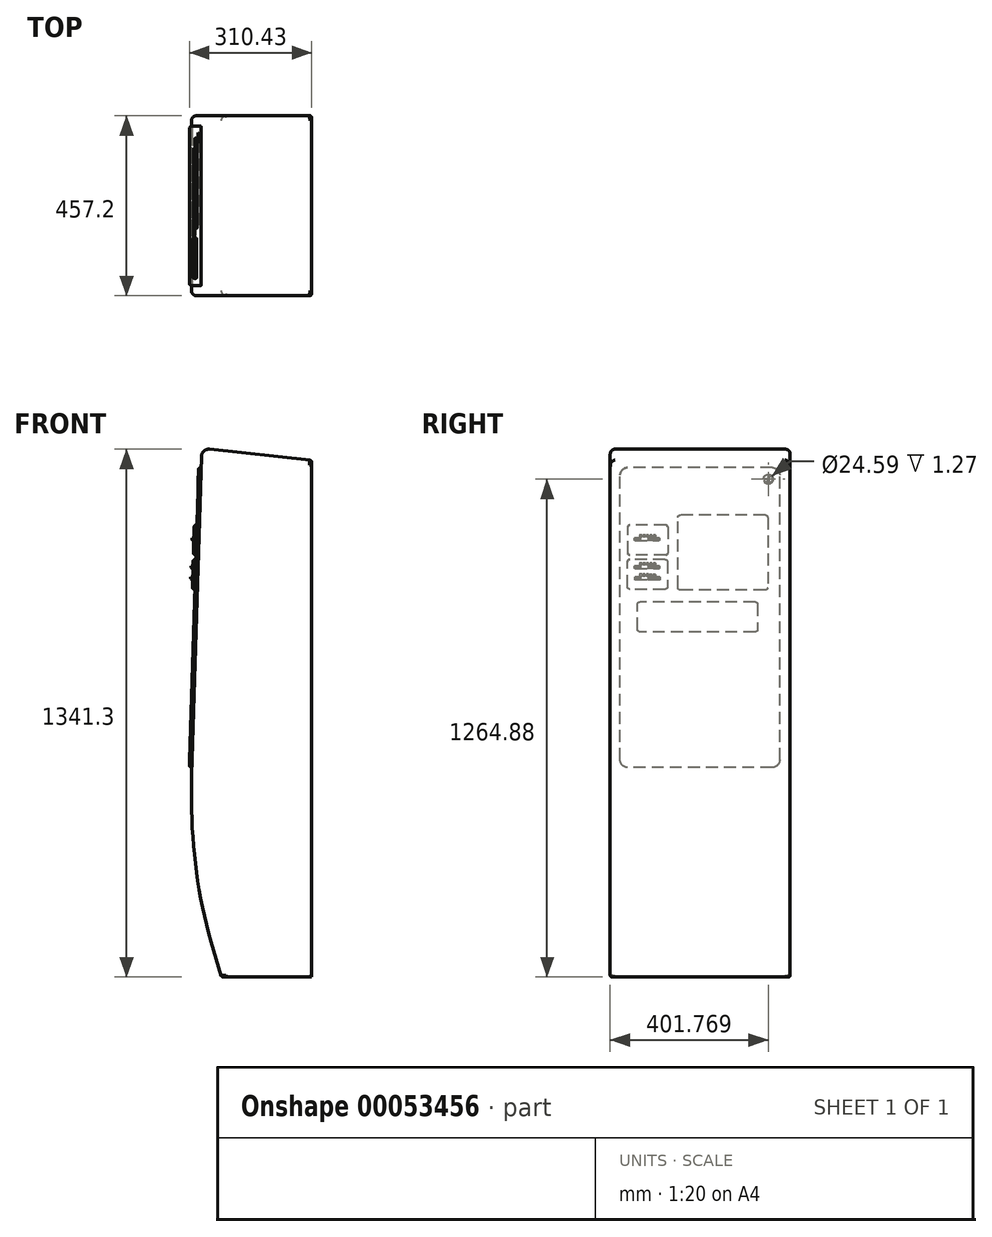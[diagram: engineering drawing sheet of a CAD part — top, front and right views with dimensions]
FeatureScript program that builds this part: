
annotation { "Feature Type Name" : "Feature", "Feature Type Description" : "" }
export const myFeature = defineFeature(function(context is Context, id is Id, definition is map)
    precondition{}
    {
        {
            var Q0;
            Q0=qCreatedBy(makeId("Front.planeOp"),FACE);
            var sketch = newSketch(context, id + "F0", { "sketchPlane" : qUnion([Q0])});
            skLineSegment(sketch, "E0", {"start": v(72.2, -154.9) * mm, "end": v(-156.4, -154.9) * mm});
            skLineSegment(sketch, "E1", {"start": v(72.04, 1157.92) * mm, "end": v(72.2, -154.9) * mm});
            skPoint(sketch, "E2.visualSharp", {"position": v(72.04, 1181.13) * mm});
            skLineSegment(sketch, "E3", {"start": v(-186.8, 1186.28) * mm, "end": v(72.04, 1157.92) * mm});
            skLineSegment(sketch, "E4", {"start": v(72.2, -154.9) * mm, "end": v(72.14, 353.1) * mm});
            skFitSpline(sketch, "E5", {"points": [v(-232.6, 359.2) * mm, v(-156.4, -154.9) * mm], "startDerivative": vector(-16.58, -646.57) * mm, "endDerivative": vector(152.32, -464.69) * mm});
            skLineSegment(sketch, "E6", {"start": v(-232.6, 359.26) * mm, "end": v(-207.9, 1167.93) * mm});
            skPoint(sketch, "E7.orphan", {"position": v(-232.6, 1191.3) * mm});
            skArc(sketch, "E8.filletArc", {"start": v(-232.6, 359.26) * mm, "mid": v(-232.6, 359.2) * mm, "end": v(-232.6, 359.13) * mm});
            skPoint(sketch, "E9.visualSharp", {"position": v(-207.28, 1188.53) * mm});
            skArc(sketch, "E9.filletArc", {"start": v(-186.8, 1186.28) * mm, "mid": v(-201.36, 1181.72) * mm, "end": v(-207.9, 1167.93) * mm});
            skSolve(sketch);
        }
        {
            var Q0;
            Q0=makeQuery(id+"F0.imprint","IMPRINT",FACE,{"disambiguationData":[TD([[makeQuery(id+"F0.imprint","IMPRINT",EDGE,{"derivedFrom":sQuery(id+"F0.wireOp",EDGE,"E0")}),-1.0]])]});
            extrude(context, id + "F1", {"entities" : qUnion([Q0]), "depth" : 457.2 * mm});
        }
        {
            var Q0;
            Q0=makeQuery(id+"F1.opExtrude","SWEPT_FACE",FACE,{"disambiguationData":[OSD([sQuery(id+"F0.wireOp",EDGE,"E6")])]});
            var sketch = newSketch(context, id + "F2", { "sketchPlane" : qUnion([Q0])});
            skLineSegment(sketch, "E10.bottom", {"start": v(45.56, 370.5) * mm, "end": v(412.75, 370.5) * mm});
            skLineSegment(sketch, "E10.top", {"start": v(45.56, 1132.5) * mm, "end": v(412.75, 1132.5) * mm});
            skLineSegment(sketch, "E10.left", {"start": v(26.5, 389.55) * mm, "end": v(26.5, 1113.45) * mm});
            skLineSegment(sketch, "E10.right", {"start": v(431.8, 389.55) * mm, "end": v(431.8, 1113.45) * mm});
            skPoint(sketch, "E11.end.orphan", {"position": v(431.8, 352) * mm});
            skLineSegment(sketch, "E12", {"start": v(0, 1161.04) * mm, "end": v(0, 1135.64) * mm});
            skPoint(sketch, "E13.visualSharp", {"position": v(26.5, 1132.5) * mm});
            skArc(sketch, "E13.filletArc", {"start": v(45.56, 1132.5) * mm, "mid": v(32.09, 1126.92) * mm, "end": v(26.5, 1113.45) * mm});
            skPoint(sketch, "E14.visualSharp", {"position": v(431.8, 1132.5) * mm});
            skArc(sketch, "E14.filletArc", {"start": v(431.8, 1113.45) * mm, "mid": v(426.22, 1126.92) * mm, "end": v(412.75, 1132.5) * mm});
            skPoint(sketch, "E15.visualSharp", {"position": v(431.8, 370.5) * mm});
            skArc(sketch, "E15.filletArc", {"start": v(412.75, 370.5) * mm, "mid": v(426.22, 376.08) * mm, "end": v(431.8, 389.55) * mm});
            skPoint(sketch, "E16.visualSharp", {"position": v(26.5, 370.5) * mm});
            skArc(sketch, "E16.filletArc", {"start": v(26.5, 389.55) * mm, "mid": v(32.09, 376.08) * mm, "end": v(45.56, 370.5) * mm});
            skSolve(sketch);
        }
        {
            var Q0;
            Q0 = qSketchRegion(id + "F2", true);
            extrude(context, id + "F3", {"entities" : qUnion([Q0]), "operationType" : NewBodyOperationType.ADD, "depth" : 6.35 * mm});
        }
        {
            var Q0;
            Q0=makeQuery(id+"F3.opExtrude","CAP_EDGE",EDGE,{"disambiguationData":[OSD([sQuery(id+"F2.wireOp",EDGE,"E10.right")])],"isStart":false});
            fillet(context, id + "F4", {"entities" : qUnion([Q0]), "radius" : 5.08 * mm, "tangentPropagation" : true, "allowEdgeOverflow" : false});
        }
        {
            var Q0;
            Q0=makeQuery(id+"F1.opExtrude","CAP_EDGE",EDGE,{"disambiguationData":[OSD([sQuery(id+"F0.wireOp",EDGE,"E6")])],"isStart":true});
            var Q1;
            Q1=makeQuery(id+"F1.opExtrude","CAP_EDGE",EDGE,{"disambiguationData":[OSD([sQuery(id+"F0.wireOp",EDGE,"E6")])],"isStart":false});
            fillet(context, id + "F5", {"entities" : qUnion([Q0, Q1]), "radius" : 12.7 * mm, "tangentPropagation" : true, "allowEdgeOverflow" : false});
        }
        {
            var Q0;
            Q0=makeQuery(id+"F3.opExtrude","CAP_FACE",FACE,{"disambiguationData":[OSD([sQuery(id+"F2.wireOp",EDGE,"E10.bottom"),sQuery(id+"F2.wireOp",EDGE,"E10.top"),sQuery(id+"F2.wireOp",EDGE,"E10.left"),sQuery(id+"F2.wireOp",EDGE,"E10.right"),sQuery(id+"F2.wireOp",EDGE,"E13.filletArc"),sQuery(id+"F2.wireOp",EDGE,"E14.filletArc"),sQuery(id+"F2.wireOp",EDGE,"E15.filletArc"),sQuery(id+"F2.wireOp",EDGE,"E16.filletArc")])],"isStart":false});
            var sketch = newSketch(context, id + "F6", { "sketchPlane" : qUnion([Q0])});
            skLineSegment(sketch, "E17", {"start": v(31.59, 1113.45) * mm, "end": v(31.59, 389.55) * mm});
            skLineSegment(sketch, "E18", {"start": v(63.34, 1011.85) * mm, "end": v(279.24, 1011.85) * mm});
            skLineSegment(sketch, "E19", {"start": v(56.99, 1005.5) * mm, "end": v(56.99, 827.7) * mm});
            skLineSegment(sketch, "E20", {"start": v(63.34, 821.35) * mm, "end": v(279.24, 821.35) * mm});
            skLineSegment(sketch, "E21", {"start": v(285.59, 827.7) * mm, "end": v(285.59, 1005.5) * mm});
            skLineSegment(sketch, "E22", {"start": v(310.99, 986.45) * mm, "end": v(412.59, 986.45) * mm});
            skLineSegment(sketch, "E23", {"start": v(310.99, 986.45) * mm, "end": v(310.99, 910.25) * mm});
            skLineSegment(sketch, "E24", {"start": v(310.99, 910.25) * mm, "end": v(412.59, 910.25) * mm});
            skLineSegment(sketch, "E25", {"start": v(412.59, 910.25) * mm, "end": v(412.59, 986.45) * mm});
            skLineSegment(sketch, "E26", {"start": v(311.6, 892.88) * mm, "end": v(311.6, 829.38) * mm});
            skLineSegment(sketch, "E27", {"start": v(317.95, 823.03) * mm, "end": v(406.85, 823.03) * mm});
            skLineSegment(sketch, "E28", {"start": v(317.95, 899.23) * mm, "end": v(406.85, 899.23) * mm});
            skLineSegment(sketch, "E29", {"start": v(413.2, 829.38) * mm, "end": v(413.2, 892.88) * mm});
            skLineSegment(sketch, "E30", {"start": v(88.74, 791.2) * mm, "end": v(381.45, 791.2) * mm});
            skLineSegment(sketch, "E31", {"start": v(82.39, 784.84) * mm, "end": v(82.39, 721.34) * mm});
            skLineSegment(sketch, "E32", {"start": v(88.74, 715) * mm, "end": v(381.45, 715) * mm});
            skLineSegment(sketch, "E33", {"start": v(387.8, 721.34) * mm, "end": v(387.8, 784.84) * mm});
            skPoint(sketch, "E34.visualSharp", {"position": v(56.99, 1011.85) * mm});
            skArc(sketch, "E34.filletArc", {"start": v(63.34, 1011.85) * mm, "mid": v(58.85, 1009.99) * mm, "end": v(56.99, 1005.5) * mm});
            skPoint(sketch, "E35.visualSharp", {"position": v(285.59, 1011.85) * mm});
            skArc(sketch, "E35.filletArc", {"start": v(285.59, 1005.5) * mm, "mid": v(283.73, 1009.99) * mm, "end": v(279.24, 1011.85) * mm});
            skPoint(sketch, "E36.visualSharp", {"position": v(285.59, 821.35) * mm});
            skArc(sketch, "E36.filletArc", {"start": v(279.24, 821.35) * mm, "mid": v(283.73, 823.2) * mm, "end": v(285.59, 827.7) * mm});
            skPoint(sketch, "E37.visualSharp", {"position": v(56.99, 821.35) * mm});
            skArc(sketch, "E37.filletArc", {"start": v(56.99, 827.7) * mm, "mid": v(58.85, 823.2) * mm, "end": v(63.34, 821.35) * mm});
            skPoint(sketch, "E38.visualSharp", {"position": v(82.39, 791.2) * mm});
            skArc(sketch, "E38.filletArc", {"start": v(88.74, 791.2) * mm, "mid": v(84.25, 789.33) * mm, "end": v(82.39, 784.84) * mm});
            skPoint(sketch, "E39.visualSharp", {"position": v(82.39, 715) * mm});
            skArc(sketch, "E39.filletArc", {"start": v(82.39, 721.34) * mm, "mid": v(84.25, 716.85) * mm, "end": v(88.74, 715) * mm});
            skPoint(sketch, "E40.visualSharp", {"position": v(387.8, 715) * mm});
            skArc(sketch, "E40.filletArc", {"start": v(381.45, 715) * mm, "mid": v(385.94, 716.85) * mm, "end": v(387.8, 721.34) * mm});
            skPoint(sketch, "E41.visualSharp", {"position": v(387.8, 791.2) * mm});
            skArc(sketch, "E41.filletArc", {"start": v(387.8, 784.84) * mm, "mid": v(385.94, 789.33) * mm, "end": v(381.45, 791.2) * mm});
            skPoint(sketch, "E42.visualSharp", {"position": v(311.6, 823.03) * mm});
            skArc(sketch, "E42.filletArc", {"start": v(311.6, 829.38) * mm, "mid": v(313.46, 824.89) * mm, "end": v(317.95, 823.03) * mm});
            skPoint(sketch, "E43.visualSharp", {"position": v(311.6, 899.23) * mm});
            skArc(sketch, "E43.filletArc", {"start": v(317.95, 899.23) * mm, "mid": v(313.46, 897.37) * mm, "end": v(311.6, 892.88) * mm});
            skPoint(sketch, "E44.visualSharp", {"position": v(413.2, 899.23) * mm});
            skArc(sketch, "E44.filletArc", {"start": v(413.2, 892.88) * mm, "mid": v(411.34, 897.37) * mm, "end": v(406.85, 899.23) * mm});
            skPoint(sketch, "E45.visualSharp", {"position": v(413.2, 823.03) * mm});
            skArc(sketch, "E45.filletArc", {"start": v(406.85, 823.03) * mm, "mid": v(411.34, 824.89) * mm, "end": v(413.2, 829.38) * mm});
            skSolve(sketch);
        }
        {
            var Q0;
            Q0=makeQuery(id+"F6.imprint","IMPRINT",FACE,{"disambiguationData":[TD([[makeQuery(id+"F6.imprint","IMPRINT",EDGE,{"derivedFrom":sQuery(id+"F6.wireOp",EDGE,"E30")}),-1.0]])]});
            var Q1;
            Q1=makeQuery(id+"F6.imprint","IMPRINT",FACE,{"disambiguationData":[TD([[makeQuery(id+"F6.imprint","IMPRINT",EDGE,{"derivedFrom":sQuery(id+"F6.wireOp",EDGE,"E18")}),-1.0]])]});
            extrude(context, id + "F7", {"entities" : qUnion([Q0, Q1]), "operationType" : NewBodyOperationType.REMOVE, "oppositeDirection" : true, "depth" : 2.54 * mm});
        }
        {
            var Q0;
            Q0=makeQuery(id+"F6.imprint","IMPRINT",FACE,{"disambiguationData":[TD([[makeQuery(id+"F6.imprint","IMPRINT",EDGE,{"derivedFrom":sQuery(id+"F6.wireOp",EDGE,"E22")}),-1.0]])]});
            var Q1;
            Q1=makeQuery(id+"F6.imprint","IMPRINT",FACE,{"disambiguationData":[TD([[makeQuery(id+"F6.imprint","IMPRINT",EDGE,{"derivedFrom":sQuery(id+"F6.wireOp",EDGE,"E26")}),1.0]])]});
            extrude(context, id + "F8", {"entities" : qUnion([Q0, Q1]), "operationType" : NewBodyOperationType.ADD, "depth" : 6.35 * mm});
        }
        {
            var Q0;
            Q0=makeQuery(id+"F8.opExtrude","CAP_EDGE",EDGE,{"disambiguationData":[OSD([sQuery(id+"F6.wireOp",EDGE,"E25")])],"isStart":false});
            var Q1;
            Q1=makeQuery(id+"F8.opExtrude","CAP_EDGE",EDGE,{"disambiguationData":[OSD([sQuery(id+"F6.wireOp",EDGE,"E22")])],"isStart":false});
            var Q2;
            Q2=makeQuery(id+"F8.opExtrude","CAP_EDGE",EDGE,{"disambiguationData":[OSD([sQuery(id+"F6.wireOp",EDGE,"E23")])],"isStart":false});
            var Q3;
            Q3=makeQuery(id+"F8.opExtrude","CAP_EDGE",EDGE,{"disambiguationData":[OSD([sQuery(id+"F6.wireOp",EDGE,"E24")])],"isStart":false});
            fillet(context, id + "F9", {"entities" : qUnion([Q0, Q1, Q2, Q3]), "radius" : 5.08 * mm, "tangentPropagation" : true, "allowEdgeOverflow" : false});
        }
        {
            var Q0;
            Q0=makeQuery(id+"F9.opFillet","BLEND_EDGE",EDGE,{"blendedFrom":[makeQuery(id+"F8.opExtrude","CAP_EDGE",EDGE,{"disambiguationData":[OSD([sQuery(id+"F6.wireOp",EDGE,"E22")])],"isStart":false}),makeQuery(id+"F8.opExtrude","CAP_EDGE",EDGE,{"disambiguationData":[OSD([sQuery(id+"F6.wireOp",EDGE,"E25")])],"isStart":false})],"blendedInto":[]});
            var Q1;
            Q1=makeQuery(id+"F9.opFillet","BLEND_EDGE",EDGE,{"blendedFrom":[makeQuery(id+"F8.opExtrude","CAP_EDGE",EDGE,{"disambiguationData":[OSD([sQuery(id+"F6.wireOp",EDGE,"E24")])],"isStart":false}),makeQuery(id+"F8.opExtrude","CAP_EDGE",EDGE,{"disambiguationData":[OSD([sQuery(id+"F6.wireOp",EDGE,"E25")])],"isStart":false})],"blendedInto":[]});
            var Q2;
            Q2=makeQuery(id+"F9.opFillet","BLEND_EDGE",EDGE,{"blendedFrom":[makeQuery(id+"F8.opExtrude","CAP_EDGE",EDGE,{"disambiguationData":[OSD([sQuery(id+"F6.wireOp",EDGE,"E23")])],"isStart":false}),makeQuery(id+"F8.opExtrude","CAP_EDGE",EDGE,{"disambiguationData":[OSD([sQuery(id+"F6.wireOp",EDGE,"E24")])],"isStart":false})],"blendedInto":[]});
            var Q3;
            Q3=makeQuery(id+"F9.opFillet","BLEND_EDGE",EDGE,{"blendedFrom":[makeQuery(id+"F8.opExtrude","CAP_EDGE",EDGE,{"disambiguationData":[OSD([sQuery(id+"F6.wireOp",EDGE,"E22")])],"isStart":false}),makeQuery(id+"F8.opExtrude","CAP_EDGE",EDGE,{"disambiguationData":[OSD([sQuery(id+"F6.wireOp",EDGE,"E23")])],"isStart":false})],"blendedInto":[]});
            fillet(context, id + "F10", {"entities" : qUnion([Q0, Q1, Q2, Q3]), "radius" : 5.08 * mm, "tangentPropagation" : true, "allowEdgeOverflow" : false});
        }
        {
            var Q0;
            Q0=makeQuery(id+"F8.opExtrude","CAP_EDGE",EDGE,{"disambiguationData":[OSD([sQuery(id+"F6.wireOp",EDGE,"E29")])],"isStart":false});
            var Q1;
            Q1=makeQuery(id+"F8.opExtrude","CAP_EDGE",EDGE,{"disambiguationData":[OSD([sQuery(id+"F6.wireOp",EDGE,"E28")])],"isStart":false});
            var Q2;
            Q2=makeQuery(id+"F8.opExtrude","CAP_EDGE",EDGE,{"disambiguationData":[OSD([sQuery(id+"F6.wireOp",EDGE,"E26")])],"isStart":false});
            var Q3;
            Q3=makeQuery(id+"F8.opExtrude","CAP_EDGE",EDGE,{"disambiguationData":[OSD([sQuery(id+"F6.wireOp",EDGE,"E27")])],"isStart":false});
            fillet(context, id + "F11", {"entities" : qUnion([Q0, Q1, Q2, Q3]), "radius" : 5.08 * mm, "tangentPropagation" : true, "allowEdgeOverflow" : false});
        }
        {
            var Q0;
            Q0=makeQuery(id+"F8.opExtrude","CAP_FACE",FACE,{"disambiguationData":[OSD([sQuery(id+"F6.wireOp",EDGE,"E22"),sQuery(id+"F6.wireOp",EDGE,"E23"),sQuery(id+"F6.wireOp",EDGE,"E24"),sQuery(id+"F6.wireOp",EDGE,"E25")])],"isStart":false});
            var sketch = newSketch(context, id + "F12", { "sketchPlane" : qUnion([Q0])});
            skLineSegment(sketch, "E46", {"start": v(331.8, 952.84) * mm, "end": v(395.3, 952.84) * mm});
            skLineSegment(sketch, "E47", {"start": v(331.8, 946.5) * mm, "end": v(395.3, 946.5) * mm});
            skLineSegment(sketch, "E48", {"start": v(395.3, 946.5) * mm, "end": v(395.3, 952.84) * mm});
            skLineSegment(sketch, "E49", {"start": v(331.8, 952.84) * mm, "end": v(331.8, 946.5) * mm});
            skPoint(sketch, "E50.startSnap0", {"position": v(331.8, 949.67) * mm});
            skLineSegment(sketch, "E51.bottom", {"start": v(332.73, 951.82) * mm, "end": v(394.27, 951.82) * mm});
            skLineSegment(sketch, "E51.top", {"start": v(332.73, 947.35) * mm, "end": v(394.27, 947.35) * mm});
            skLineSegment(sketch, "E51.left", {"start": v(332.73, 951.82) * mm, "end": v(332.73, 947.35) * mm});
            skLineSegment(sketch, "E51.right", {"start": v(394.27, 951.82) * mm, "end": v(394.27, 947.35) * mm});
            skSolve(sketch);
        }
        {
            var Q0;
            Q0=makeQuery(id+"F8.opExtrude","CAP_FACE",FACE,{"disambiguationData":[OSD([sQuery(id+"F6.wireOp",EDGE,"E26"),sQuery(id+"F6.wireOp",EDGE,"E27"),sQuery(id+"F6.wireOp",EDGE,"E28"),sQuery(id+"F6.wireOp",EDGE,"E29"),sQuery(id+"F6.wireOp",EDGE,"E42.filletArc"),sQuery(id+"F6.wireOp",EDGE,"E43.filletArc"),sQuery(id+"F6.wireOp",EDGE,"E44.filletArc"),sQuery(id+"F6.wireOp",EDGE,"E45.filletArc")])],"isStart":false});
            var sketch = newSketch(context, id + "F13", { "sketchPlane" : qUnion([Q0])});
            skLineSegment(sketch, "E52", {"start": v(331.36, 881.57) * mm, "end": v(394.86, 881.57) * mm});
            skLineSegment(sketch, "E53", {"start": v(331.36, 875.22) * mm, "end": v(394.86, 875.22) * mm});
            skLineSegment(sketch, "E54", {"start": v(394.86, 875.22) * mm, "end": v(394.86, 881.57) * mm});
            skLineSegment(sketch, "E55", {"start": v(331.36, 881.57) * mm, "end": v(331.36, 875.22) * mm});
            skPoint(sketch, "E56.startSnap0", {"position": v(331.36, 878.4) * mm});
            skLineSegment(sketch, "E57.bottom", {"start": v(332.28, 880.55) * mm, "end": v(393.83, 880.55) * mm});
            skLineSegment(sketch, "E57.top", {"start": v(332.28, 876.08) * mm, "end": v(393.83, 876.08) * mm});
            skLineSegment(sketch, "E57.left", {"start": v(332.28, 880.55) * mm, "end": v(332.28, 876.08) * mm});
            skLineSegment(sketch, "E57.right", {"start": v(393.83, 880.55) * mm, "end": v(393.83, 876.08) * mm});
            skLineSegment(sketch, "E58", {"start": v(331.2, 853.46) * mm, "end": v(394.7, 853.46) * mm});
            skLineSegment(sketch, "E59", {"start": v(331.2, 847.11) * mm, "end": v(394.7, 847.11) * mm});
            skLineSegment(sketch, "E60", {"start": v(394.7, 847.11) * mm, "end": v(394.7, 853.46) * mm});
            skLineSegment(sketch, "E61", {"start": v(331.2, 853.46) * mm, "end": v(331.2, 847.11) * mm});
            skPoint(sketch, "E62.startSnap0", {"position": v(331.2, 850.29) * mm});
            skLineSegment(sketch, "E63.bottom", {"start": v(332.13, 852.44) * mm, "end": v(393.68, 852.44) * mm});
            skLineSegment(sketch, "E63.top", {"start": v(332.13, 847.97) * mm, "end": v(393.68, 847.97) * mm});
            skLineSegment(sketch, "E63.left", {"start": v(332.13, 852.44) * mm, "end": v(332.13, 847.97) * mm});
            skLineSegment(sketch, "E63.right", {"start": v(393.68, 852.44) * mm, "end": v(393.68, 847.97) * mm});
            skSolve(sketch);
        }
        {
            var Q0;
            Q0 = qSketchRegion(id + "F12", true);
            extrude(context, id + "F14", {"entities" : qUnion([Q0]), "operationType" : NewBodyOperationType.ADD, "depth" : 5.08 * mm});
        }
        {
            var Q0;
            Q0 = qSketchRegion(id + "F13", true);
            extrude(context, id + "F15", {"entities" : qUnion([Q0]), "operationType" : NewBodyOperationType.ADD, "depth" : 5.08 * mm});
        }
        {
            var Q0;
            Q0=makeQuery(id+"F14.opExtrude","CAP_EDGE",EDGE,{"disambiguationData":[OSD([sQuery(id+"F12.wireOp",EDGE,"E47")])],"isStart":false});
            fillet(context, id + "F16", {"entities" : qUnion([Q0]), "radius" : 5.08 * mm, "tangentPropagation" : true, "allowEdgeOverflow" : false});
        }
        {
            var Q0;
            Q0=makeQuery(id+"F15.opExtrude","CAP_EDGE",EDGE,{"disambiguationData":[OSD([sQuery(id+"F13.wireOp",EDGE,"E53")])],"isStart":false});
            fillet(context, id + "F17", {"entities" : qUnion([Q0]), "radius" : 5.08 * mm, "tangentPropagation" : true, "allowEdgeOverflow" : false});
        }
        {
            var Q0;
            Q0=makeQuery(id+"F15.opExtrude","CAP_EDGE",EDGE,{"disambiguationData":[OSD([sQuery(id+"F13.wireOp",EDGE,"E59")])],"isStart":false});
            var Q1;
            Q1=makeQuery(id+"F1.opExtrude","CAP_FACE",FACE,{"disambiguationData":[OSD([sQuery(id+"F0.wireOp",EDGE,"E0"),sQuery(id+"F0.wireOp",EDGE,"E1"),sQuery(id+"F0.wireOp",EDGE,"E3"),sQuery(id+"F0.wireOp",EDGE,"E4"),sQuery(id+"F0.wireOp",EDGE,"E5"),sQuery(id+"F0.wireOp",EDGE,"E6"),sQuery(id+"F0.wireOp",EDGE,"E8.filletArc"),sQuery(id+"F0.wireOp",EDGE,"E9.filletArc")])],"isStart":false});
            fillet(context, id + "F18", {"entities" : qUnion([Q0, Q1]), "radius" : 5.08 * mm, "tangentPropagation" : true, "allowEdgeOverflow" : false});
        }
        {
            var Q0;
            Q0=makeQuery(id+"F3.opExtrude","CAP_FACE",FACE,{"disambiguationData":[OSD([sQuery(id+"F2.wireOp",EDGE,"E10.bottom"),sQuery(id+"F2.wireOp",EDGE,"E10.top"),sQuery(id+"F2.wireOp",EDGE,"E10.left"),sQuery(id+"F2.wireOp",EDGE,"E10.right"),sQuery(id+"F2.wireOp",EDGE,"E13.filletArc"),sQuery(id+"F2.wireOp",EDGE,"E14.filletArc"),sQuery(id+"F2.wireOp",EDGE,"E15.filletArc"),sQuery(id+"F2.wireOp",EDGE,"E16.filletArc")])],"isStart":false});
            var sketch = newSketch(context, id + "F19", { "sketchPlane" : qUnion([Q0])});
            skCircle(sketch, "E64", {"center": v(55.43, 1102.9) * mm, "radius": 12.3 * mm});
            skArc(sketch, "E65", {"start": v(55.43, 1114.1) * mm, "mid": v(47.9, 1094.72) * mm, "end": v(67.03, 1102.9) * mm});
            skArc(sketch, "E66", {"start": v(55.43, 1113.61) * mm, "mid": v(48.4, 1095.51) * mm, "end": v(66.35, 1102.9) * mm});
            skLineSegment(sketch, "E67", {"start": v(55.43, 1114.1) * mm, "end": v(55.43, 1113.61) * mm});
            skLineSegment(sketch, "E68", {"start": v(66.35, 1102.9) * mm, "end": v(56.55, 1102.9) * mm});
            skLineSegment(sketch, "E69", {"start": v(56.55, 1102.9) * mm, "end": v(56.55, 1103.59) * mm});
            skLineSegment(sketch, "E70", {"start": v(56.55, 1103.59) * mm, "end": v(66.96, 1103.59) * mm});
            skLineSegment(sketch, "E71", {"start": v(66.96, 1103.59) * mm, "end": v(67.03, 1102.9) * mm});
            skLineSegment(sketch, "E72", {"start": v(54.5, 1110.92) * mm, "end": v(54.5, 1097.18) * mm});
            skLineSegment(sketch, "E73", {"start": v(54.5, 1097.18) * mm, "end": v(59.02, 1097.18) * mm});
            skLineSegment(sketch, "E74", {"start": v(59.02, 1097.18) * mm, "end": v(59.02, 1098.24) * mm});
            skLineSegment(sketch, "E75", {"start": v(59.02, 1098.24) * mm, "end": v(55.48, 1098.24) * mm});
            skLineSegment(sketch, "E76", {"start": v(55.48, 1098.24) * mm, "end": v(55.48, 1110.92) * mm});
            skCircle(sketch, "E77", {"center": v(51.16, 1109.43) * mm, "radius": 1.49 * mm});
            skLineSegment(sketch, "E78", {"start": v(54.5, 1110.92) * mm, "end": v(55.48, 1110.92) * mm});
            skSolve(sketch);
        }
        {
            var Q0;
            Q0 = qSketchRegion(id + "F19", true);
            extrude(context, id + "F20", {"entities" : qUnion([Q0]), "operationType" : NewBodyOperationType.REMOVE, "oppositeDirection" : true, "depth" : 1.27 * mm});
        }
        {
            var Q0;
            {var subQ0=sQuery(id+"F6.wireOp",EDGE,"E24");var subQ1=sQuery(id+"F6.wireOp",EDGE,"E25");var subQ3=sQuery(id+"F6.wireOp",EDGE,"E22");var subQ5=sQuery(id+"F6.wireOp",EDGE,"E23");Q0=makeQuery(id+"F14.boolean.opBoolean","SPLIT",FACE,{"disambiguationData":[TD([makeQuery(id+"F9.opFillet","BLEND_FACE",FACE,{"disambiguationData":[OSD([subQ3])]})])],"derivedFrom":makeQuery(id+"F8.opExtrude","CAP_FACE",FACE,{"disambiguationData":[OSD([subQ3,subQ5,subQ0,subQ1])],"isStart":false})});}
            var sketch = newSketch(context, id + "F21", { "sketchPlane" : qUnion([Q0])});
            skLineSegment(sketch, "E79.bottom", {"start": v(342.05, 960.67) * mm, "end": v(347.53, 960.67) * mm});
            skLineSegment(sketch, "E79.top", {"start": v(342.05, 955.2) * mm, "end": v(347.53, 955.2) * mm});
            skLineSegment(sketch, "E79.left", {"start": v(342.05, 960.67) * mm, "end": v(342.05, 955.2) * mm});
            skLineSegment(sketch, "E79.right", {"start": v(347.53, 960.67) * mm, "end": v(347.53, 955.2) * mm});
            skLineSegment(sketch, "E80.bottom", {"start": v(350.72, 960.67) * mm, "end": v(356.66, 960.67) * mm});
            skLineSegment(sketch, "E80.top", {"start": v(350.72, 955.2) * mm, "end": v(356.66, 955.2) * mm});
            skLineSegment(sketch, "E80.left", {"start": v(350.72, 960.67) * mm, "end": v(350.72, 955.2) * mm});
            skLineSegment(sketch, "E80.right", {"start": v(356.66, 960.67) * mm, "end": v(356.66, 955.2) * mm});
            skLineSegment(sketch, "E81.bottom", {"start": v(359.4, 961.13) * mm, "end": v(365.1, 961.13) * mm});
            skLineSegment(sketch, "E81.top", {"start": v(359.4, 955.42) * mm, "end": v(365.1, 955.42) * mm});
            skLineSegment(sketch, "E81.left", {"start": v(359.4, 961.13) * mm, "end": v(359.4, 955.42) * mm});
            skLineSegment(sketch, "E81.right", {"start": v(365.1, 961.13) * mm, "end": v(365.1, 955.42) * mm});
            skLineSegment(sketch, "E82.bottom", {"start": v(368.06, 961.13) * mm, "end": v(373.54, 961.13) * mm});
            skLineSegment(sketch, "E82.top", {"start": v(368.06, 955.65) * mm, "end": v(373.54, 955.65) * mm});
            skLineSegment(sketch, "E82.left", {"start": v(368.06, 961.13) * mm, "end": v(368.06, 955.65) * mm});
            skLineSegment(sketch, "E82.right", {"start": v(373.54, 961.13) * mm, "end": v(373.54, 955.65) * mm});
            skLineSegment(sketch, "E83.bottom", {"start": v(376.28, 961.13) * mm, "end": v(382.44, 961.13) * mm});
            skLineSegment(sketch, "E83.top", {"start": v(376.28, 955.42) * mm, "end": v(382.44, 955.42) * mm});
            skLineSegment(sketch, "E83.left", {"start": v(376.28, 961.13) * mm, "end": v(376.28, 955.42) * mm});
            skLineSegment(sketch, "E83.right", {"start": v(382.44, 961.13) * mm, "end": v(382.44, 955.42) * mm});
            skLineSegment(sketch, "E84.bottom", {"start": v(342, 889.9) * mm, "end": v(347.48, 889.9) * mm});
            skLineSegment(sketch, "E84.top", {"start": v(342, 884.43) * mm, "end": v(347.48, 884.43) * mm});
            skLineSegment(sketch, "E84.left", {"start": v(342, 889.9) * mm, "end": v(342, 884.43) * mm});
            skLineSegment(sketch, "E84.right", {"start": v(347.48, 889.9) * mm, "end": v(347.48, 884.43) * mm});
            skLineSegment(sketch, "E85.bottom", {"start": v(350.68, 889.9) * mm, "end": v(356.6, 889.9) * mm});
            skLineSegment(sketch, "E85.top", {"start": v(350.68, 884.43) * mm, "end": v(356.6, 884.43) * mm});
            skLineSegment(sketch, "E85.left", {"start": v(350.68, 889.9) * mm, "end": v(350.68, 884.43) * mm});
            skLineSegment(sketch, "E85.right", {"start": v(356.6, 889.9) * mm, "end": v(356.6, 884.43) * mm});
            skLineSegment(sketch, "E86.bottom", {"start": v(359.35, 890.36) * mm, "end": v(365.05, 890.36) * mm});
            skLineSegment(sketch, "E86.top", {"start": v(359.35, 884.66) * mm, "end": v(365.05, 884.66) * mm});
            skLineSegment(sketch, "E86.left", {"start": v(359.35, 890.36) * mm, "end": v(359.35, 884.66) * mm});
            skLineSegment(sketch, "E86.right", {"start": v(365.05, 890.36) * mm, "end": v(365.05, 884.66) * mm});
            skLineSegment(sketch, "E87.bottom", {"start": v(368.02, 890.36) * mm, "end": v(373.5, 890.36) * mm});
            skLineSegment(sketch, "E87.top", {"start": v(368.02, 884.89) * mm, "end": v(373.5, 884.89) * mm});
            skLineSegment(sketch, "E87.left", {"start": v(368.02, 890.36) * mm, "end": v(368.02, 884.89) * mm});
            skLineSegment(sketch, "E87.right", {"start": v(373.5, 890.36) * mm, "end": v(373.5, 884.89) * mm});
            skLineSegment(sketch, "E88.bottom", {"start": v(376.23, 890.36) * mm, "end": v(382.4, 890.36) * mm});
            skLineSegment(sketch, "E88.top", {"start": v(376.23, 884.66) * mm, "end": v(382.4, 884.66) * mm});
            skLineSegment(sketch, "E88.left", {"start": v(376.23, 890.36) * mm, "end": v(376.23, 884.66) * mm});
            skLineSegment(sketch, "E88.right", {"start": v(382.4, 890.36) * mm, "end": v(382.4, 884.66) * mm});
            skLineSegment(sketch, "E89.bottom", {"start": v(342.46, 860.92) * mm, "end": v(347.94, 860.92) * mm});
            skLineSegment(sketch, "E89.top", {"start": v(342.46, 855.44) * mm, "end": v(347.94, 855.44) * mm});
            skLineSegment(sketch, "E89.left", {"start": v(342.46, 860.92) * mm, "end": v(342.46, 855.44) * mm});
            skLineSegment(sketch, "E89.right", {"start": v(347.94, 860.92) * mm, "end": v(347.94, 855.44) * mm});
            skLineSegment(sketch, "E90.bottom", {"start": v(351.13, 860.92) * mm, "end": v(357.07, 860.92) * mm});
            skLineSegment(sketch, "E90.top", {"start": v(351.13, 855.44) * mm, "end": v(357.07, 855.44) * mm});
            skLineSegment(sketch, "E90.left", {"start": v(351.13, 860.92) * mm, "end": v(351.13, 855.44) * mm});
            skLineSegment(sketch, "E90.right", {"start": v(357.07, 860.92) * mm, "end": v(357.07, 855.44) * mm});
            skLineSegment(sketch, "E91.bottom", {"start": v(359.8, 861.37) * mm, "end": v(365.5, 861.37) * mm});
            skLineSegment(sketch, "E91.top", {"start": v(359.8, 855.67) * mm, "end": v(365.5, 855.67) * mm});
            skLineSegment(sketch, "E91.left", {"start": v(359.8, 861.37) * mm, "end": v(359.8, 855.67) * mm});
            skLineSegment(sketch, "E91.right", {"start": v(365.5, 861.37) * mm, "end": v(365.5, 855.67) * mm});
            skLineSegment(sketch, "E92.bottom", {"start": v(368.48, 861.37) * mm, "end": v(373.95, 861.37) * mm});
            skLineSegment(sketch, "E92.top", {"start": v(368.48, 855.9) * mm, "end": v(373.95, 855.9) * mm});
            skLineSegment(sketch, "E92.left", {"start": v(368.48, 861.37) * mm, "end": v(368.48, 855.9) * mm});
            skLineSegment(sketch, "E92.right", {"start": v(373.95, 861.37) * mm, "end": v(373.95, 855.9) * mm});
            skLineSegment(sketch, "E93.bottom", {"start": v(376.69, 861.37) * mm, "end": v(382.85, 861.37) * mm});
            skLineSegment(sketch, "E93.top", {"start": v(376.69, 855.67) * mm, "end": v(382.85, 855.67) * mm});
            skLineSegment(sketch, "E93.left", {"start": v(376.69, 861.37) * mm, "end": v(376.69, 855.67) * mm});
            skLineSegment(sketch, "E93.right", {"start": v(382.85, 861.37) * mm, "end": v(382.85, 855.67) * mm});
            skSolve(sketch);
        }
        {
            var Q0;
            Q0=makeQuery(id+"F21.imprint","IMPRINT",FACE,{"disambiguationData":[TD([[makeQuery(id+"F21.imprint","IMPRINT",EDGE,{"derivedFrom":sQuery(id+"F21.wireOp",EDGE,"E84.bottom")}),-1.0]])]});
            var Q1;
            Q1=makeQuery(id+"F21.imprint","IMPRINT",FACE,{"disambiguationData":[TD([[makeQuery(id+"F21.imprint","IMPRINT",EDGE,{"derivedFrom":sQuery(id+"F21.wireOp",EDGE,"E85.bottom")}),-1.0]])]});
            var Q2;
            Q2=makeQuery(id+"F21.imprint","IMPRINT",FACE,{"disambiguationData":[TD([[makeQuery(id+"F21.imprint","IMPRINT",EDGE,{"derivedFrom":sQuery(id+"F21.wireOp",EDGE,"E86.bottom")}),-1.0]])]});
            var Q3;
            Q3=makeQuery(id+"F21.imprint","IMPRINT",FACE,{"disambiguationData":[TD([[makeQuery(id+"F21.imprint","IMPRINT",EDGE,{"derivedFrom":sQuery(id+"F21.wireOp",EDGE,"E87.bottom")}),-1.0]])]});
            var Q4;
            Q4=makeQuery(id+"F21.imprint","IMPRINT",FACE,{"disambiguationData":[TD([[makeQuery(id+"F21.imprint","IMPRINT",EDGE,{"derivedFrom":sQuery(id+"F21.wireOp",EDGE,"E88.bottom")}),-1.0]])]});
            var Q5;
            Q5=makeQuery(id+"F21.imprint","IMPRINT",FACE,{"disambiguationData":[TD([[makeQuery(id+"F21.imprint","IMPRINT",EDGE,{"derivedFrom":sQuery(id+"F21.wireOp",EDGE,"E89.bottom")}),-1.0]])]});
            var Q6;
            Q6=makeQuery(id+"F21.imprint","IMPRINT",FACE,{"disambiguationData":[TD([[makeQuery(id+"F21.imprint","IMPRINT",EDGE,{"derivedFrom":sQuery(id+"F21.wireOp",EDGE,"E90.bottom")}),-1.0]])]});
            var Q7;
            Q7=makeQuery(id+"F21.imprint","IMPRINT",FACE,{"disambiguationData":[TD([[makeQuery(id+"F21.imprint","IMPRINT",EDGE,{"derivedFrom":sQuery(id+"F21.wireOp",EDGE,"E91.bottom")}),-1.0]])]});
            var Q8;
            Q8=makeQuery(id+"F21.imprint","IMPRINT",FACE,{"disambiguationData":[TD([[makeQuery(id+"F21.imprint","IMPRINT",EDGE,{"derivedFrom":sQuery(id+"F21.wireOp",EDGE,"E92.bottom")}),-1.0]])]});
            var Q9;
            Q9=makeQuery(id+"F21.imprint","IMPRINT",FACE,{"disambiguationData":[TD([[makeQuery(id+"F21.imprint","IMPRINT",EDGE,{"derivedFrom":sQuery(id+"F21.wireOp",EDGE,"E93.bottom")}),-1.0]])]});
            var Q10;
            Q10=makeQuery(id+"F21.imprint","IMPRINT",FACE,{"disambiguationData":[TD([[makeQuery(id+"F21.imprint","IMPRINT",EDGE,{"derivedFrom":sQuery(id+"F21.wireOp",EDGE,"E79.bottom")}),-1.0]])]});
            var Q11;
            Q11=makeQuery(id+"F21.imprint","IMPRINT",FACE,{"disambiguationData":[TD([[makeQuery(id+"F21.imprint","IMPRINT",EDGE,{"derivedFrom":sQuery(id+"F21.wireOp",EDGE,"E80.bottom")}),-1.0]])]});
            var Q12;
            Q12=makeQuery(id+"F21.imprint","IMPRINT",FACE,{"disambiguationData":[TD([[makeQuery(id+"F21.imprint","IMPRINT",EDGE,{"derivedFrom":sQuery(id+"F21.wireOp",EDGE,"E81.bottom")}),-1.0]])]});
            var Q13;
            Q13=makeQuery(id+"F21.imprint","IMPRINT",FACE,{"disambiguationData":[TD([[makeQuery(id+"F21.imprint","IMPRINT",EDGE,{"derivedFrom":sQuery(id+"F21.wireOp",EDGE,"E82.bottom")}),-1.0]])]});
            var Q14;
            Q14=makeQuery(id+"F21.imprint","IMPRINT",FACE,{"disambiguationData":[TD([[makeQuery(id+"F21.imprint","IMPRINT",EDGE,{"derivedFrom":sQuery(id+"F21.wireOp",EDGE,"E83.bottom")}),-1.0]])]});
            extrude(context, id + "F22", {"entities" : qUnion([Q0, Q1, Q2, Q3, Q4, Q5, Q6, Q7, Q8, Q9, Q10, Q11, Q12, Q13, Q14]), "operationType" : NewBodyOperationType.REMOVE, "oppositeDirection" : true, "depth" : 1.27 * mm});
        }
    });
